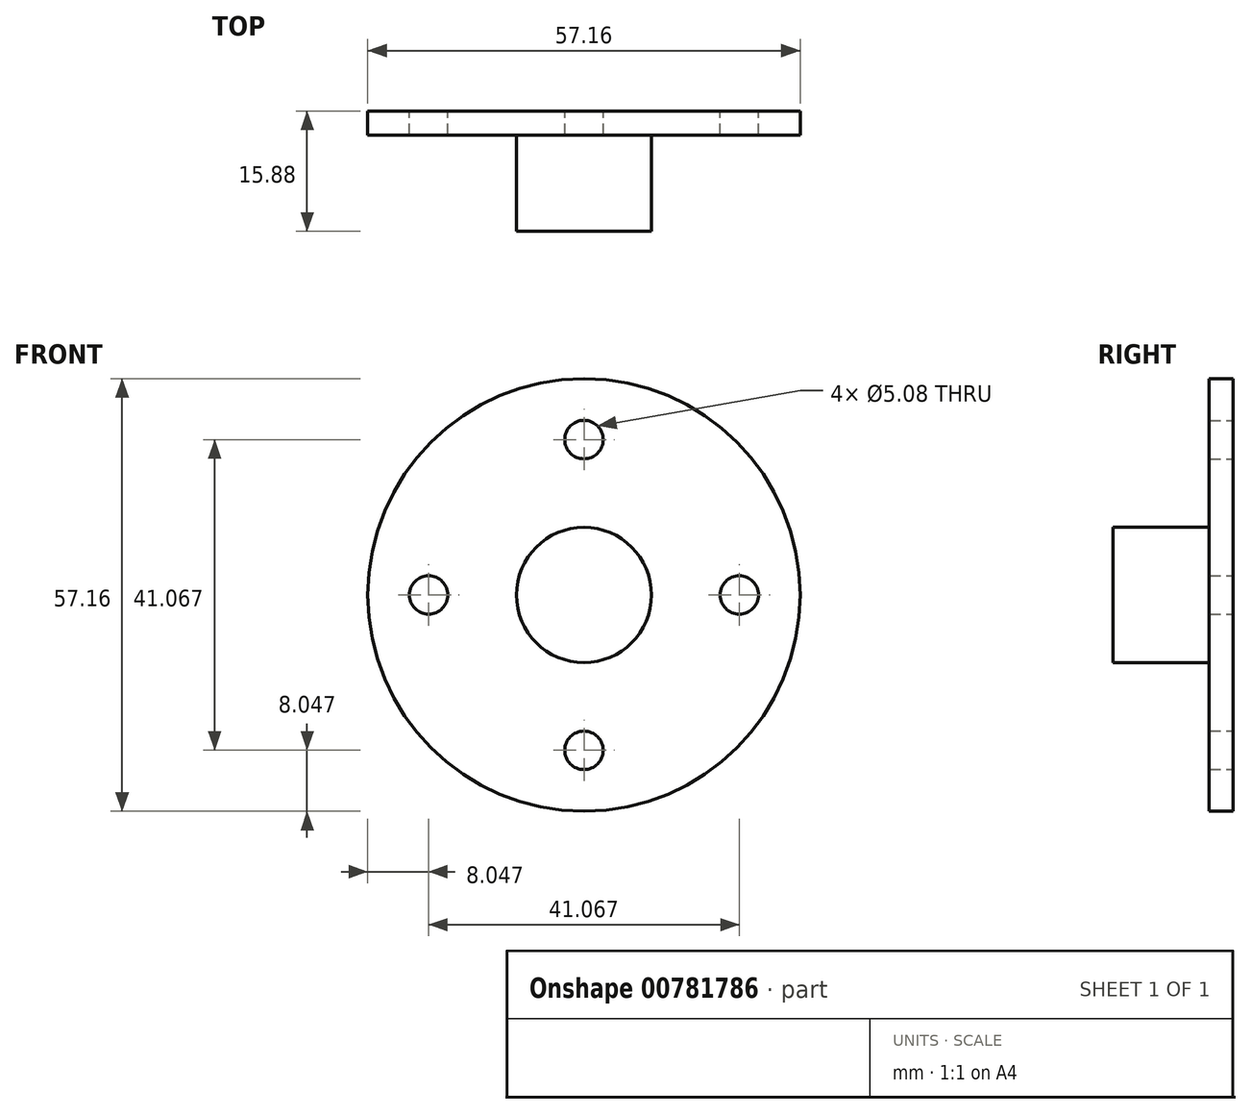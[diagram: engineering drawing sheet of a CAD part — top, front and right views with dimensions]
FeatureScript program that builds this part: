
annotation { "Feature Type Name" : "Feature", "Feature Type Description" : "" }
export const myFeature = defineFeature(function(context is Context, id is Id, definition is map)
    precondition{}
    {
        {
            var Q0;
            Q0=qCreatedBy(makeId("Front.planeOp"),FACE);
            var sketch = newSketch(context, id + "F0", { "sketchPlane" : qUnion([Q0])});
            skCircle(sketch, "E0", {"center": v(0, 0) * mm, "radius": 28.57 * mm});
            skCircle(sketch, "E1", {"center": v(0, 0) * mm, "radius": 12.7 * mm});
            skCircle(sketch, "E2", {"center": v(56.36, 0) * mm, "radius": 2.08 * mm});
            skCircle(sketch, "E3", {"center": v(0, 20.53) * mm, "radius": 2.54 * mm});
            skCircle(sketch, "E4.1.0", {"center": v(-20.53, 0) * mm, "radius": 2.54 * mm});
            skCircle(sketch, "E4.2.0", {"center": v(0, -20.53) * mm, "radius": 2.54 * mm});
            skCircle(sketch, "E4.3.0", {"center": v(20.53, 0) * mm, "radius": 2.54 * mm});
            skSolve(sketch);
        }
        {
            var Q0;
            Q0=makeQuery(id+"F0.imprint","IMPRINT",FACE,{"disambiguationData":[TD([[makeQuery(id+"F0.imprint","IMPRINT",EDGE,{"derivedFrom":sQuery(id+"F0.wireOp",EDGE,"E0")}),1.0]])]});
            var Q1;
            Q1=makeQuery(id+"F0.imprint","IMPRINT",FACE,{"disambiguationData":[TD([[makeQuery(id+"F0.imprint","IMPRINT",EDGE,{"derivedFrom":sQuery(id+"F0.wireOp",EDGE,"E1")}),1.0]])]});
            extrude(context, id + "F1", {"entities" : qUnion([Q0, Q1]), "depth" : 3.17 * mm, "offsetDistance" : 25.4 * mm});
        }
        {
            var Q0;
            Q0=makeQuery(id+"F1.opExtrude","CAP_FACE",FACE,{"disambiguationData":[OSD([sQuery(id+"F0.wireOp",EDGE,"E0"),sQuery(id+"F0.wireOp",EDGE,"E3"),sQuery(id+"F0.wireOp",EDGE,"E4.1.0"),sQuery(id+"F0.wireOp",EDGE,"E4.2.0"),sQuery(id+"F0.wireOp",EDGE,"E4.3.0")])],"isStart":false});
            var sketch = newSketch(context, id + "F2", { "sketchPlane" : qUnion([Q0])});
            skCircle(sketch, "E5", {"center": v(0, 0) * mm, "radius": 8.93 * mm});
            skSolve(sketch);
        }
        {
            var Q0;
            Q0=makeQuery(id+"F2.imprint","IMPRINT",FACE,{"disambiguationData":[TD([[makeQuery(id+"F2.imprint","IMPRINT",EDGE,{"derivedFrom":sQuery(id+"F2.wireOp",EDGE,"E5")}),1.0]])]});
            extrude(context, id + "F3", {"entities" : qUnion([Q0]), "operationType" : NewBodyOperationType.ADD, "depth" : 12.7 * mm, "offsetDistance" : 25.4 * mm});
        }
    });
